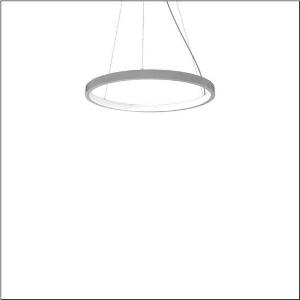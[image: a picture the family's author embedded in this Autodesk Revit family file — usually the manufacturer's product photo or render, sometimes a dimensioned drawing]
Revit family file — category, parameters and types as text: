
# Revit family: silica_r__21_ring-i_5pjbi2d3204a_c88e
name_source: partatom
category: Lighting Fixtures
units: mm (PartAtom-declared; Revit-internal decimal feet)

## family parameters
Cut with Voids When Loaded = No
Host = Face
Light Source = No
Part Type = Normal
Room Calculation Point = No
Round Connector Dimension = Use Diameter
Shared = No

## types (1)
- Silica® 21 Ring-I (1 x LED, 5040 lm, 80 W, 4000K)
    Apparent Load = 80 VA
    CIE Flux Codes = 22 48 76 50 101
    Color Rendering = 80
    Color Temperature = 4000K
    Default Elevation = 1800 mm
    Description = Silica® 21 Ring-I, suspended luminaire, of PMMA, frosted, light emission: inner ring side luminous distribution, primary light characteristic: symmetric, installation type: suspended mounting, LED, rated luminous flux: 5.040lm, luminous efficacy: 63lm/W, light colour: 840, colour temperature: 4000K, with terminal, 5-pole, mains connection: 230V, AC/DC, 0/50..60Hz, rated input power: 80W, housing, of extruded aluminium section, metallic grey (RAL 9006), diameter: 805mm, ceiling canopy, metallic grey (RAL 9006), protection rating (lamp compartment): IP40, insulation class (complete): insulation class I (protective earthing), certification: CE, impact resistance: IK02, permissible operating ambient temperature: 0..+35°C, packaging unit: 1 piece
    Height = 48 mm  [stored 0.15748 ft]
    Lamp = 1 x LED
    Lamp Light Flux = 5040 lm
    Lamp Power = 80 W
    Lamp count = 1
    Length = 805 mm
    Luminous efficacy = 63 lm/W
    Manufacturer = Siteco
    ModVariant = No
    Model = 5PJBI2D3204A
    Mounting Place = Ceiling
    Mounting Type = Pendant
    Number of Poles = 1
    OnlyDefault = Yes
    Power Factor = 1
    Product Name = Silica® 21 Ring-I
    Product group = suspended luminaire
    ProductGroupID = 904
    Protection Class = Protection class I
    Protection Degree = IP 40
    RLX_Detail_Level = 1
    RLX_Emergency_Light_Flux = 0 lm
    RLX_Emergency_Type = 0
    RLX_Emergency_Type_DB = No
    RlxData = <blob elided: 13101 chars, md5=5c324e39>
    Socket = socket
    Standby Power = 0 W
    System Light Flux = 5040 lm
    System Power = 80 W
    Type Comments = Product without accessories
    Type Image = l_1251752.jpg
    URL = http://relux.com
    VarID = ---
    Voltage = 0 V
    Weight = 0.00 kg
    Width = 0 mm  [stored 0 ft]

note: [stored X ft] marks values corroborated as IEEE doubles in the binary element streams (Revit-internal decimal feet)

## geometry (parser evidence)
native form markers: Sweep x13
no freeform markers — native parametric forms only
